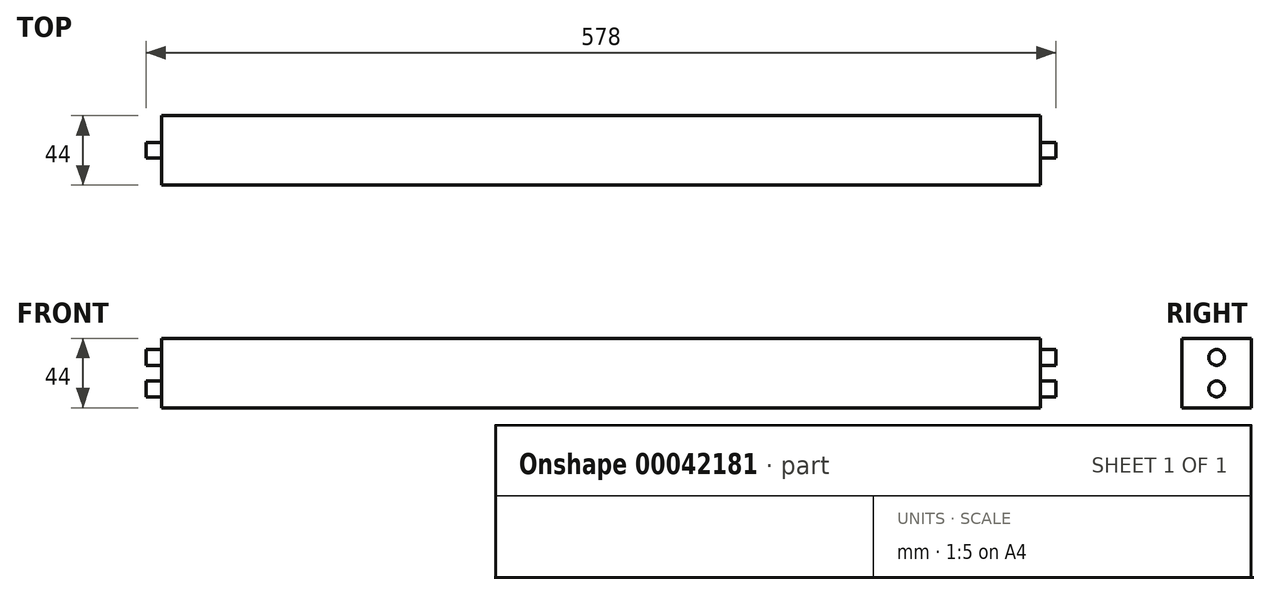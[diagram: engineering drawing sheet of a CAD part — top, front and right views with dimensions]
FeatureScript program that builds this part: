
annotation { "Feature Type Name" : "Feature", "Feature Type Description" : "" }
export const myFeature = defineFeature(function(context is Context, id is Id, definition is map)
    precondition{}
    {
        {
            var Q0;
            Q0=qCreatedBy(makeId("Top.planeOp"),FACE);
            var sketch = newSketch(context, id + "F0", { "sketchPlane" : qUnion([Q0])});
            skLineSegment(sketch, "E0", {"start": v(0, 0) * mm, "end": v(558, 0) * mm});
            skLineSegment(sketch, "E1", {"start": v(558, 0) * mm, "end": v(558, 44) * mm});
            skLineSegment(sketch, "E2", {"start": v(558, 44) * mm, "end": v(0, 44) * mm});
            skLineSegment(sketch, "E3", {"start": v(0, 44) * mm, "end": v(0, 0) * mm});
            skSolve(sketch);
        }
        {
            var Q0;
            Q0=makeQuery(id+"F0.imprint","IMPRINT",FACE,{"disambiguationData":[TD([[makeQuery(id+"F0.imprint","IMPRINT",EDGE,{"derivedFrom":sQuery(id+"F0.wireOp",EDGE,"E0")}),1.0]])]});
            extrude(context, id + "F1", {"entities" : qUnion([Q0]), "depth" : 44 * mm});
        }
        {
            var Q0;
            Q0=makeQuery(id+"F1.opExtrude","SWEPT_FACE",FACE,{"disambiguationData":[OSD([sQuery(id+"F0.wireOp",EDGE,"E3")])]});
            var sketch = newSketch(context, id + "F2", { "sketchPlane" : qUnion([Q0])});
            skCircle(sketch, "E4", {"center": v(-22, 32) * mm, "radius": 5 * mm});
            skCircle(sketch, "E5.0.1.0", {"center": v(-22, 12) * mm, "radius": 5 * mm});
            skLineSegment(sketch, "E5.direction1", {"start": v(-22, 32) * mm, "end": v(15, 32) * mm, "construction": true});
            skLineSegment(sketch, "E5.direction2", {"start": v(-22, 32) * mm, "end": v(-22, 12) * mm, "construction": true});
            skSolve(sketch);
        }
        {
            var Q0;
            Q0=makeQuery(id+"F2.imprint","IMPRINT",FACE,{"disambiguationData":[TD([[makeQuery(id+"F2.imprint","IMPRINT",EDGE,{"derivedFrom":sQuery(id+"F2.wireOp",EDGE,"E4")}),1.0]])]});
            var Q1;
            Q1=makeQuery(id+"F2.imprint","IMPRINT",FACE,{"disambiguationData":[TD([[makeQuery(id+"F2.imprint","IMPRINT",EDGE,{"derivedFrom":sQuery(id+"F2.wireOp",EDGE,"E5.0.1.0")}),1.0]])]});
            extrude(context, id + "F3", {"entities" : qUnion([Q0, Q1]), "operationType" : NewBodyOperationType.ADD, "depth" : 10 * mm, "hasSecondDirection" : true, "secondDirectionOppositeDirection" : true, "secondDirectionDepth" : 568 * mm});
        }
    });
